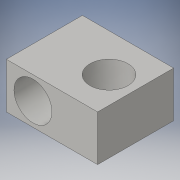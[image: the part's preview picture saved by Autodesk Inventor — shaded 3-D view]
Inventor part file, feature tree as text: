
AUTODESK INVENTOR PART (.ipt)
format: ipt  version: 2016 (Build 200138000, 138)  size: 104,960 bytes
history: native  units: in
note: dims shown in document units (in); Inventor stores cm internally (conversion verified against a paired STEP export)
features: extrude x3, sketch x3
ambient origin geometry x8: Origin, YZ Plane, XZ Plane, XY Plane, X Axis, Y Axis, Z Axis, Center Point
bodies: Solid1 (feature_tree)
feature tree (6):
  extrude  "Extrusion1"  Depth=1.0in
  extrude  "Extrusion4"  Depth=0.6in
  extrude  "Extrusion5"  Depth=1.0in TaperAngle=0.0deg
  sketch  "Sketch1"  dims[d0=1.2in d1=1.0in]
  sketch  "Sketch4"  dims[d2=0.6in d3=0.0in d14=0.5in]
  sketch  "Sketch5"  dims[d15=0.35in d16=1.0in d17=0.0in d18=0.5in d19=0.35in d20=0.6in d21=0.0in]
